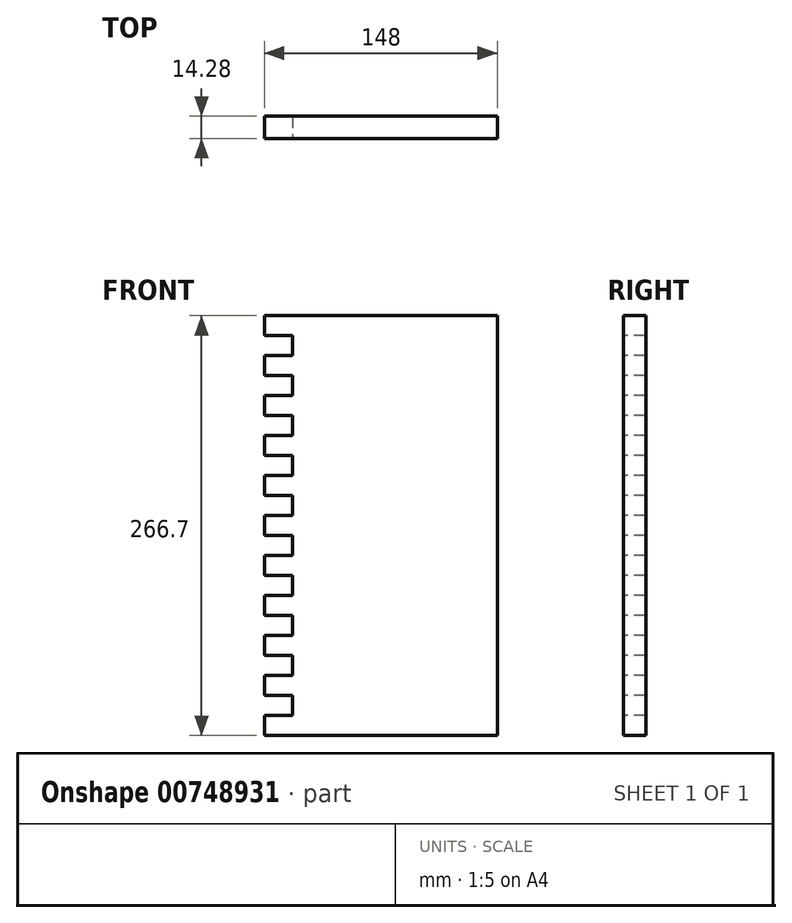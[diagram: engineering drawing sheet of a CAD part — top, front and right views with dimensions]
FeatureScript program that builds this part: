
annotation { "Feature Type Name" : "Feature", "Feature Type Description" : "" }
export const myFeature = defineFeature(function(context is Context, id is Id, definition is map)
    precondition{}
    {
        {
            var Q0;
            Q0=qCreatedBy(makeId("Top.planeOp"),FACE);
            var sketch = newSketch(context, id + "F0", { "sketchPlane" : qUnion([Q0])});
            skLineSegment(sketch, "E0.top", {"start": v(-32.17, -4.4) * mm, "end": v(-180.17, -4.4) * mm});
            skLineSegment(sketch, "E0.right", {"start": v(-180.17, 9.88) * mm, "end": v(-180.17, -4.4) * mm});
            skLineSegment(sketch, "E1", {"start": v(-32.17, 9.88) * mm, "end": v(-32.17, -4.4) * mm});
            skLineSegment(sketch, "E2", {"start": v(-180.17, 9.88) * mm, "end": v(-32.17, 9.88) * mm});
            skSolve(sketch);
        }
        {
            var Q0;
            Q0=makeQuery(id+"F0.imprint","IMPRINT",FACE,{"disambiguationData":[TD([[makeQuery(id+"F0.imprint","IMPRINT",EDGE,{"derivedFrom":sQuery(id+"F0.wireOp",EDGE,"E0.top")}),-1.0]])]});
            extrude(context, id + "F1", {"entities" : qUnion([Q0]), "oppositeDirection" : true, "depth" : 266.7 * mm, "offsetDistance" : 25 * mm, "symmetric" : true});
        }
        {
            var Q0;
            Q0=makeQuery(id+"F1.opExtrude","SWEPT_FACE",FACE,{"disambiguationData":[OSD([sQuery(id+"F0.wireOp",EDGE,"E0.top")])]});
            var sketch = newSketch(context, id + "F2", { "sketchPlane" : qUnion([Q0])});
            skPoint(sketch, "E3.endSnap0", {"position": v(-106.17, 133.35) * mm});
            skLineSegment(sketch, "E4", {"start": v(0, 0) * mm, "end": v(260, 0) * mm});
            skLineSegment(sketch, "E5", {"start": v(-121.5, -133.35) * mm, "end": v(-121.5, -101.4) * mm});
            skLineSegment(sketch, "E6", {"start": v(-121.5, -101.4) * mm, "end": v(-46.2, -101.4) * mm});
            skLineSegment(sketch, "E7.MirrorCS", {"start": v(-399.5, -120.65) * mm, "end": v(-399.5, -107.95) * mm});
            skLineSegment(sketch, "E8.MirrorCS", {"start": v(-381.5, -120.65) * mm, "end": v(-381.5, -107.95) * mm});
            skLineSegment(sketch, "E9.MirrorCS", {"start": v(-381.5, -95.25) * mm, "end": v(-399.5, -95.25) * mm});
            skLineSegment(sketch, "E10.MirrorCS", {"start": v(-399.5, -95.25) * mm, "end": v(-399.5, -82.55) * mm});
            skLineSegment(sketch, "E11.MirrorCS", {"start": v(-265, 120.65) * mm, "end": v(-283, 120.65) * mm});
            skLineSegment(sketch, "E12.MirrorCS", {"start": v(-381.5, -69.85) * mm, "end": v(-399.5, -69.85) * mm});
            skLineSegment(sketch, "E13.MirrorCS", {"start": v(-399.5, -82.55) * mm, "end": v(-381.5, -82.55) * mm});
            skLineSegment(sketch, "E14.MirrorCS", {"start": v(-399.5, -120.65) * mm, "end": v(-399.5, -133.35) * mm});
            skLineSegment(sketch, "E15.MirrorCS", {"start": v(-283, 69.85) * mm, "end": v(-283, 57.15) * mm});
            skLineSegment(sketch, "E16.MirrorCS", {"start": v(-283, 95.25) * mm, "end": v(-283, 107.95) * mm});
            skLineSegment(sketch, "E17.MirrorCS", {"start": v(-399.5, -44.45) * mm, "end": v(-399.5, -57.15) * mm});
            skLineSegment(sketch, "E18.MirrorCS", {"start": v(-399.5, -57.15) * mm, "end": v(-381.5, -57.15) * mm});
            skLineSegment(sketch, "E19.MirrorCS", {"start": v(-399.5, -107.95) * mm, "end": v(-381.5, -107.95) * mm});
            skLineSegment(sketch, "E20.MirrorCS", {"start": v(-283, 57.15) * mm, "end": v(-265, 57.15) * mm});
            skLineSegment(sketch, "E21.MirrorCS", {"start": v(-265, 95.25) * mm, "end": v(-265, 82.55) * mm});
            skLineSegment(sketch, "E22.MirrorCS", {"start": v(-283, 19.05) * mm, "end": v(-265, 19.05) * mm});
            skLineSegment(sketch, "E23.MirrorCS", {"start": v(-265, 44.45) * mm, "end": v(-283, 44.45) * mm});
            skLineSegment(sketch, "E24.MirrorCS", {"start": v(-283, 44.45) * mm, "end": v(-283, 57.15) * mm});
            skLineSegment(sketch, "E25.MirrorCS", {"start": v(-265, 19.05) * mm, "end": v(-265, 6.35) * mm});
            skLineSegment(sketch, "E26.MirrorCS", {"start": v(-399.5, -95.25) * mm, "end": v(-399.5, -107.95) * mm});
            skLineSegment(sketch, "E27.MirrorCS", {"start": v(-265, 95.25) * mm, "end": v(-283, 95.25) * mm});
            skLineSegment(sketch, "E28.MirrorCS", {"start": v(-283, 19.05) * mm, "end": v(-283, 6.35) * mm});
            skLineSegment(sketch, "E29.MirrorCS", {"start": v(-399.5, -69.85) * mm, "end": v(-399.5, -57.15) * mm});
            skLineSegment(sketch, "E30.MirrorCS", {"start": v(-265, 44.45) * mm, "end": v(-265, 31.75) * mm});
            skLineSegment(sketch, "E31.MirrorCS", {"start": v(-399.5, -31.75) * mm, "end": v(-381.5, -31.75) * mm});
            skLineSegment(sketch, "E32.MirrorCS", {"start": v(-399.5, -19.05) * mm, "end": v(-381.5, -19.05) * mm});
            skLineSegment(sketch, "E33.MirrorCS", {"start": v(-399.5, -19.05) * mm, "end": v(-399.5, -31.75) * mm});
            skLineSegment(sketch, "E34.MirrorCS", {"start": v(-265, 120.65) * mm, "end": v(-265, 107.95) * mm});
            skLineSegment(sketch, "E35.MirrorCS", {"start": v(-283, 19.05) * mm, "end": v(-283, 31.75) * mm});
            skLineSegment(sketch, "E36.MirrorCS", {"start": v(-265, 69.85) * mm, "end": v(-283, 69.85) * mm});
            skLineSegment(sketch, "E37.MirrorCS", {"start": v(-265, 69.85) * mm, "end": v(-265, 57.15) * mm});
            skLineSegment(sketch, "E38.MirrorCS", {"start": v(-381.5, -44.45) * mm, "end": v(-399.5, -44.45) * mm});
            skLineSegment(sketch, "E39.MirrorCS", {"start": v(-283, 82.55) * mm, "end": v(-265, 82.55) * mm});
            skLineSegment(sketch, "E40.MirrorCS", {"start": v(-283, 44.45) * mm, "end": v(-283, 31.75) * mm});
            skLineSegment(sketch, "E41.MirrorCS", {"start": v(-381.5, -19.05) * mm, "end": v(-381.5, -6.35) * mm});
            skLineSegment(sketch, "E42.MirrorCS", {"start": v(-399.5, -44.45) * mm, "end": v(-399.5, -31.75) * mm});
            skLineSegment(sketch, "E43.MirrorCS", {"start": v(-283, 95.25) * mm, "end": v(-283, 82.55) * mm});
            skLineSegment(sketch, "E44.MirrorCS", {"start": v(-399.5, -133.35) * mm, "end": v(-381.5, -133.35) * mm});
            skLineSegment(sketch, "E45.MirrorCS", {"start": v(-283, 120.65) * mm, "end": v(-283, 133.35) * mm});
            skLineSegment(sketch, "E46.MirrorCS", {"start": v(-283, 31.75) * mm, "end": v(-265, 31.75) * mm});
            skLineSegment(sketch, "E47.MirrorCS", {"start": v(-381.5, -120.65) * mm, "end": v(-399.5, -120.65) * mm});
            skLineSegment(sketch, "E48.MirrorCS", {"start": v(-399.5, -69.85) * mm, "end": v(-399.5, -82.55) * mm});
            skLineSegment(sketch, "E49.MirrorCS", {"start": v(-381.5, -44.45) * mm, "end": v(-381.5, -31.75) * mm});
            skLineSegment(sketch, "E50.MirrorCS", {"start": v(-381.5, -6.35) * mm, "end": v(-399.5, -6.35) * mm});
            skLineSegment(sketch, "E51.MirrorCS", {"start": v(-283, 120.65) * mm, "end": v(-283, 107.95) * mm});
            skLineSegment(sketch, "E52.MirrorCS", {"start": v(-283, 133.35) * mm, "end": v(-265, 133.35) * mm});
            skLineSegment(sketch, "E53.MirrorCS", {"start": v(-265, 6.35) * mm, "end": v(-283, 6.35) * mm});
            skLineSegment(sketch, "E54.MirrorCS", {"start": v(-381.5, -95.25) * mm, "end": v(-381.5, -82.55) * mm});
            skLineSegment(sketch, "E55.MirrorCS", {"start": v(-283, 107.95) * mm, "end": v(-265, 107.95) * mm});
            skLineSegment(sketch, "E56.MirrorCS", {"start": v(-381.5, -69.85) * mm, "end": v(-381.5, -57.15) * mm});
            skLineSegment(sketch, "E57.MirrorCS", {"start": v(-399.5, -19.05) * mm, "end": v(-399.5, -6.35) * mm});
            skLineSegment(sketch, "E58.MirrorCS", {"start": v(-283, 69.85) * mm, "end": v(-283, 82.55) * mm});
            skLineSegment(sketch, "E59", {"start": v(-106.17, 133.35) * mm, "end": v(-106.17, 48.35) * mm});
            skLineSegment(sketch, "E60", {"start": v(-265, 33.35) * mm, "end": v(-265, 48.35) * mm});
            skLineSegment(sketch, "E61", {"start": v(-265, 113.35) * mm, "end": v(-265, 120.65) * mm});
            skLineSegment(sketch, "E62.bottom", {"start": v(-180.17, 133.35) * mm, "end": v(-162.17, 133.35) * mm});
            skLineSegment(sketch, "E62.top", {"start": v(-180.17, 120.65) * mm, "end": v(-162.17, 120.65) * mm});
            skLineSegment(sketch, "E62.right", {"start": v(-162.17, 133.35) * mm, "end": v(-162.17, 120.65) * mm});
            skLineSegment(sketch, "E63.left", {"start": v(-180.17, 120.65) * mm, "end": v(-180.17, 107.95) * mm});
            skLineSegment(sketch, "E63.right", {"start": v(-162.17, 120.65) * mm, "end": v(-162.17, 107.95) * mm});
            skLineSegment(sketch, "E64.bottom", {"start": v(-180.17, 107.95) * mm, "end": v(-162.17, 107.95) * mm});
            skLineSegment(sketch, "E64.top", {"start": v(-180.17, 107.95) * mm, "end": v(-162.17, 107.95) * mm});
            skLineSegment(sketch, "E64.left", {"start": v(-180.17, 107.95) * mm, "end": v(-180.17, 107.95) * mm});
            skLineSegment(sketch, "E64.right", {"start": v(-162.17, 107.95) * mm, "end": v(-162.17, 107.95) * mm});
            skLineSegment(sketch, "E65.right", {"start": v(-162.17, 107.95) * mm, "end": v(-162.17, 95.25) * mm});
            skLineSegment(sketch, "E66.bottom", {"start": v(-181.5, 95.25) * mm, "end": v(-163.5, 95.25) * mm});
            skLineSegment(sketch, "E67.bottom", {"start": v(-162.17, 95.25) * mm, "end": v(-180.17, 95.25) * mm});
            skLineSegment(sketch, "E67.left", {"start": v(-162.17, 95.25) * mm, "end": v(-162.17, 82.55) * mm});
            skLineSegment(sketch, "E67.right", {"start": v(-180.17, 95.25) * mm, "end": v(-180.17, 82.55) * mm});
            skLineSegment(sketch, "E68.bottom", {"start": v(-180.17, 82.55) * mm, "end": v(-162.17, 82.55) * mm});
            skLineSegment(sketch, "E68.top", {"start": v(-181.5, 69.85) * mm, "end": v(-162.17, 69.85) * mm});
            skLineSegment(sketch, "E68.right", {"start": v(-162.17, 82.55) * mm, "end": v(-162.17, 69.85) * mm});
            skLineSegment(sketch, "E69.bottom", {"start": v(-162.17, 69.85) * mm, "end": v(-180.17, 69.85) * mm});
            skLineSegment(sketch, "E69.left", {"start": v(-162.17, 69.85) * mm, "end": v(-162.17, 57.15) * mm});
            skLineSegment(sketch, "E69.right", {"start": v(-180.17, 69.85) * mm, "end": v(-180.17, 57.15) * mm});
            skLineSegment(sketch, "E70", {"start": v(-180.17, 0) * mm, "end": v(-52.54, 0) * mm});
            skLineSegment(sketch, "E71.bottom", {"start": v(-162.17, 57.15) * mm, "end": v(-180.17, 57.15) * mm});
            skLineSegment(sketch, "E71.top", {"start": v(-162.17, 44.45) * mm, "end": v(-180.17, 44.45) * mm});
            skLineSegment(sketch, "E71.left", {"start": v(-162.17, 57.15) * mm, "end": v(-162.17, 44.45) * mm});
            skLineSegment(sketch, "E72.left", {"start": v(-162.17, 44.45) * mm, "end": v(-162.17, 31.75) * mm});
            skLineSegment(sketch, "E72.right", {"start": v(-180.17, 44.45) * mm, "end": v(-180.17, 31.75) * mm});
            skLineSegment(sketch, "E73.bottom", {"start": v(-162.17, 31.75) * mm, "end": v(-180.17, 31.75) * mm});
            skLineSegment(sketch, "E73.left", {"start": v(-162.17, 31.75) * mm, "end": v(-162.17, 31.75) * mm});
            skLineSegment(sketch, "E73.right", {"start": v(-180.17, 31.75) * mm, "end": v(-180.17, 31.75) * mm});
            skLineSegment(sketch, "E74.top", {"start": v(-162.17, 19.05) * mm, "end": v(-180.17, 19.05) * mm});
            skLineSegment(sketch, "E74.left", {"start": v(-162.17, 31.75) * mm, "end": v(-162.17, 19.05) * mm});
            skLineSegment(sketch, "E75.bottom", {"start": v(-180.17, 19.05) * mm, "end": v(-162.17, 19.05) * mm});
            skLineSegment(sketch, "E75.left", {"start": v(-180.17, 19.05) * mm, "end": v(-180.17, 6.35) * mm});
            skLineSegment(sketch, "E75.right", {"start": v(-162.17, 19.05) * mm, "end": v(-162.17, 6.35) * mm});
            skLineSegment(sketch, "E76.bottom", {"start": v(-162.17, 6.35) * mm, "end": v(-180.17, 6.35) * mm});
            skLineSegment(sketch, "E76.top", {"start": v(-162.17, -6.35) * mm, "end": v(-180.17, -6.35) * mm});
            skLineSegment(sketch, "E76.left", {"start": v(-162.17, 6.35) * mm, "end": v(-162.17, -6.35) * mm});
            skLineSegment(sketch, "E77.MirrorCS", {"start": v(-180.17, -107.95) * mm, "end": v(-162.17, -107.95) * mm});
            skLineSegment(sketch, "E78.MirrorCS", {"start": v(-180.17, -19.05) * mm, "end": v(-162.17, -19.05) * mm});
            skLineSegment(sketch, "E79.MirrorCS", {"start": v(-162.17, -69.85) * mm, "end": v(-180.17, -69.85) * mm});
            skLineSegment(sketch, "E80.MirrorCS", {"start": v(-162.17, -95.25) * mm, "end": v(-180.17, -95.25) * mm});
            skLineSegment(sketch, "E81.MirrorCS", {"start": v(-162.17, -57.15) * mm, "end": v(-162.17, -44.45) * mm});
            skLineSegment(sketch, "E82.MirrorCS", {"start": v(-162.17, -31.75) * mm, "end": v(-180.17, -31.75) * mm});
            skLineSegment(sketch, "E83.MirrorCS", {"start": v(-180.17, -120.65) * mm, "end": v(-162.17, -120.65) * mm});
            skLineSegment(sketch, "E84.MirrorCS", {"start": v(-162.17, -31.75) * mm, "end": v(-162.17, -19.05) * mm});
            skLineSegment(sketch, "E85.MirrorCS", {"start": v(-162.17, -44.45) * mm, "end": v(-180.17, -44.45) * mm});
            skLineSegment(sketch, "E86.MirrorCS", {"start": v(-162.17, -120.65) * mm, "end": v(-162.17, -107.95) * mm});
            skLineSegment(sketch, "E87.MirrorCS", {"start": v(-180.17, -120.65) * mm, "end": v(-180.17, -107.95) * mm});
            skLineSegment(sketch, "E88.MirrorCS", {"start": v(-180.17, -19.05) * mm, "end": v(-180.17, -6.35) * mm});
            skLineSegment(sketch, "E89.MirrorCS", {"start": v(-181.5, -95.25) * mm, "end": v(-163.5, -95.25) * mm});
            skLineSegment(sketch, "E90.MirrorCS", {"start": v(-180.17, -44.45) * mm, "end": v(-180.17, -31.75) * mm});
            skLineSegment(sketch, "E91.MirrorCS", {"start": v(-180.17, -69.85) * mm, "end": v(-180.17, -57.15) * mm});
            skLineSegment(sketch, "E92.MirrorCS", {"start": v(-180.17, -133.35) * mm, "end": v(-162.17, -133.35) * mm});
            skLineSegment(sketch, "E93.MirrorCS", {"start": v(-181.5, -69.85) * mm, "end": v(-162.17, -69.85) * mm});
            skLineSegment(sketch, "E94.MirrorCS", {"start": v(-162.17, -19.05) * mm, "end": v(-180.17, -19.05) * mm});
            skLineSegment(sketch, "E95.MirrorCS", {"start": v(-180.17, -82.55) * mm, "end": v(-162.17, -82.55) * mm});
            skLineSegment(sketch, "E96.MirrorCS", {"start": v(-162.17, -19.05) * mm, "end": v(-162.17, -6.35) * mm});
            skLineSegment(sketch, "E97.MirrorCS", {"start": v(-162.17, -107.95) * mm, "end": v(-162.17, -95.25) * mm});
            skLineSegment(sketch, "E98.MirrorCS", {"start": v(-162.17, -133.35) * mm, "end": v(-162.17, -120.65) * mm});
            skLineSegment(sketch, "E99.MirrorCS", {"start": v(-162.17, -44.45) * mm, "end": v(-162.17, -31.75) * mm});
            skLineSegment(sketch, "E100.MirrorCS", {"start": v(-162.17, -57.15) * mm, "end": v(-180.17, -57.15) * mm});
            skLineSegment(sketch, "E101.MirrorCS", {"start": v(-162.17, -82.55) * mm, "end": v(-162.17, -69.85) * mm});
            skLineSegment(sketch, "E102.MirrorCS", {"start": v(-180.17, -95.25) * mm, "end": v(-180.17, -82.55) * mm});
            skLineSegment(sketch, "E103.MirrorCS", {"start": v(-162.17, -69.85) * mm, "end": v(-162.17, -57.15) * mm});
            skLineSegment(sketch, "E104.MirrorCS", {"start": v(-162.17, -95.25) * mm, "end": v(-162.17, -82.55) * mm});
            skSolve(sketch);
        }
        {
            var Q0;
            Q0=qSketchRegion(id+"F2",true);
            extrude(context, id + "F3", {"entities" : qUnion([Q0]), "operationType" : NewBodyOperationType.REMOVE, "endBound" : BoundingType.THROUGH_ALL, "oppositeDirection" : true, "depth" : 25 * mm, "offsetDistance" : 25 * mm});
        }
    });
